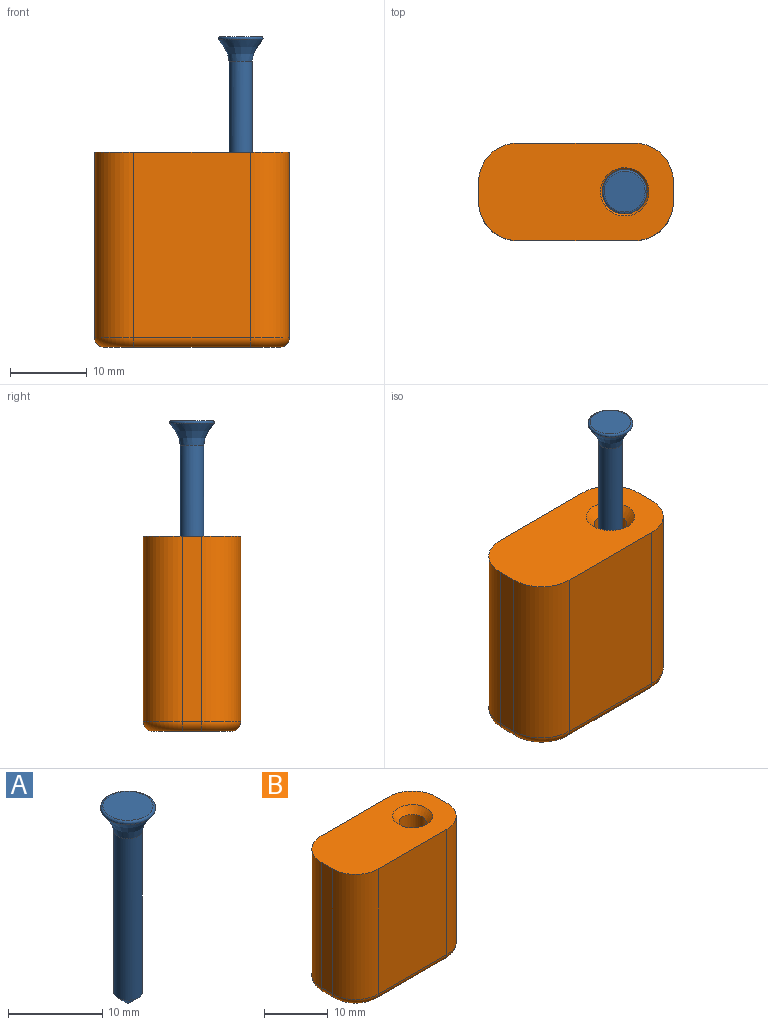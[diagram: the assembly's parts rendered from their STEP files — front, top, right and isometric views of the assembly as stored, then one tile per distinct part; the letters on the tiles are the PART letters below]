
ASSEMBLY  parts=2 mates=1
PART A: 7 faces, bbox 6.4x6.4x25.4 mm
  f0: cylinder r=1.52mm len=20.96mm, axis (0,0,-1), area 200.7mm2, adj f3,f4
  f1: plane 0.3x0.3mm, normal (0,0,-1), area 0.1mm2, adj f5
  f2: plane 5.31x5.31mm, normal (0,0,1), area 22.1mm2, adj f6
  f3: bspline ~6.35x6.35mm, area 40.1mm2, adj f0,f6
  f4: cone r=1.52mm half-angle=45deg, axis (0,0,1), area 9.8mm2, adj f0,f5
  f5: torus R=0.15mm, axis (0,0,1), area 0.3mm2, adj f1,f4
  f6: bspline ~6.35x6.35mm, area 10.1mm2, adj f2,f3
PART B: 27 faces, bbox 26.2x13.5x25.4 mm
  f0: plane 22.86x10.16mm, normal (0,0,-1), area 168.9mm2, adj f7,f10,f12,f13,f14,f15,f17,f19
  f1: plane 24.13x15.24mm, normal (0,1,0), area 367.7mm2, adj f5,f12,f16,f22
  f2: plane 24.13x2.54mm, normal (-1,0,0), area 61.3mm2, adj f5,f13,f20,f22
  f3: plane 24.13x15.24mm, normal (0,-1,0), area 367.7mm2, adj f5,f15,f18,f20
  f4: plane 24.13x2.54mm, normal (1,0,0), area 61.3mm2, adj f5,f14,f16,f18
  f5: plane 25.4x12.7mm, normal (0,0,1), area 269.3mm2, adj f1,f2,f3,f4,f16,f18,f20,f22
  f6: cylinder r=1.83mm len=8.66mm, axis (0,0,-1), area 99.5mm2, adj f7,f8
  f7: cone r=1.83mm half-angle=41deg, axis (0,0,-1), area 22.7mm2, adj f0,f6
  f8: cone r=0mm half-angle=59deg, axis (0,0,-1), area 12.3mm2, adj f6
  f9: cylinder r=1.83mm len=18.19mm, axis (0,0,-1), area 209mm2, adj f10,f11
  f10: cone r=1.83mm half-angle=41deg, axis (0,0,-1), area 22.7mm2, adj f0,f9
  f11: cone r=0mm half-angle=59deg, axis (0,0,-1), area 12.3mm2, adj f9
  f12: cylinder r=1.27mm len=15.24mm, axis (-1,0,0), area 30.4mm2, adj f0,f1,f17,f23
  f13: cylinder r=1.27mm len=2.54mm, axis (0,-1,0), area 5.1mm2, adj f0,f2,f21,f23
  f14: cylinder r=1.27mm len=2.54mm, axis (0,1,0), area 5.1mm2, adj f0,f4,f17,f19
  f15: cylinder r=1.27mm len=15.24mm, axis (1,0,0), area 30.4mm2, adj f0,f3,f19,f21
  f16: cylinder r=5.08mm len=24.13mm, axis (0,0,-1), area 192.5mm2, adj f1,f4,f5,f17
  f17: torus R=3.81mm, axis (0,0,1), area 14.5mm2, adj f0,f12,f14,f16
  f18: cylinder r=5.08mm len=24.13mm, axis (0,0,1), area 192.5mm2, adj f3,f4,f5,f19
  f19: torus R=3.81mm, axis (0,0,1), area 14.5mm2, adj f0,f14,f15,f18
  f20: cylinder r=5.08mm len=24.13mm, axis (0,0,-1), area 192.5mm2, adj f2,f3,f5,f21
  f21: torus R=3.81mm, axis (0,0,1), area 14.5mm2, adj f0,f13,f15,f20
  f22: cylinder r=5.08mm len=24.13mm, axis (0,0,1), area 192.5mm2, adj f1,f2,f5,f23
  f23: torus R=3.81mm, axis (0,0,1), area 14.5mm2, adj f0,f12,f13,f22
  f24: cylinder r=2.13mm len=8.97mm, axis (0,0,1), area 120.2mm2, adj f25,f26
  f25: cone r=2.13mm half-angle=41deg, axis (0,0,1), area 25.7mm2, adj f5,f24
  f26: cone r=0mm half-angle=59deg, axis (0,0,1), area 16.7mm2, adj f24
PLACE A t=(-22.88,6.35,15.07)mm
PLACE B at identity fixed
MATE slider A.f0 <-> B.f6  axis (0,0,-1) through (-22.88,6.35,26.82)mm
